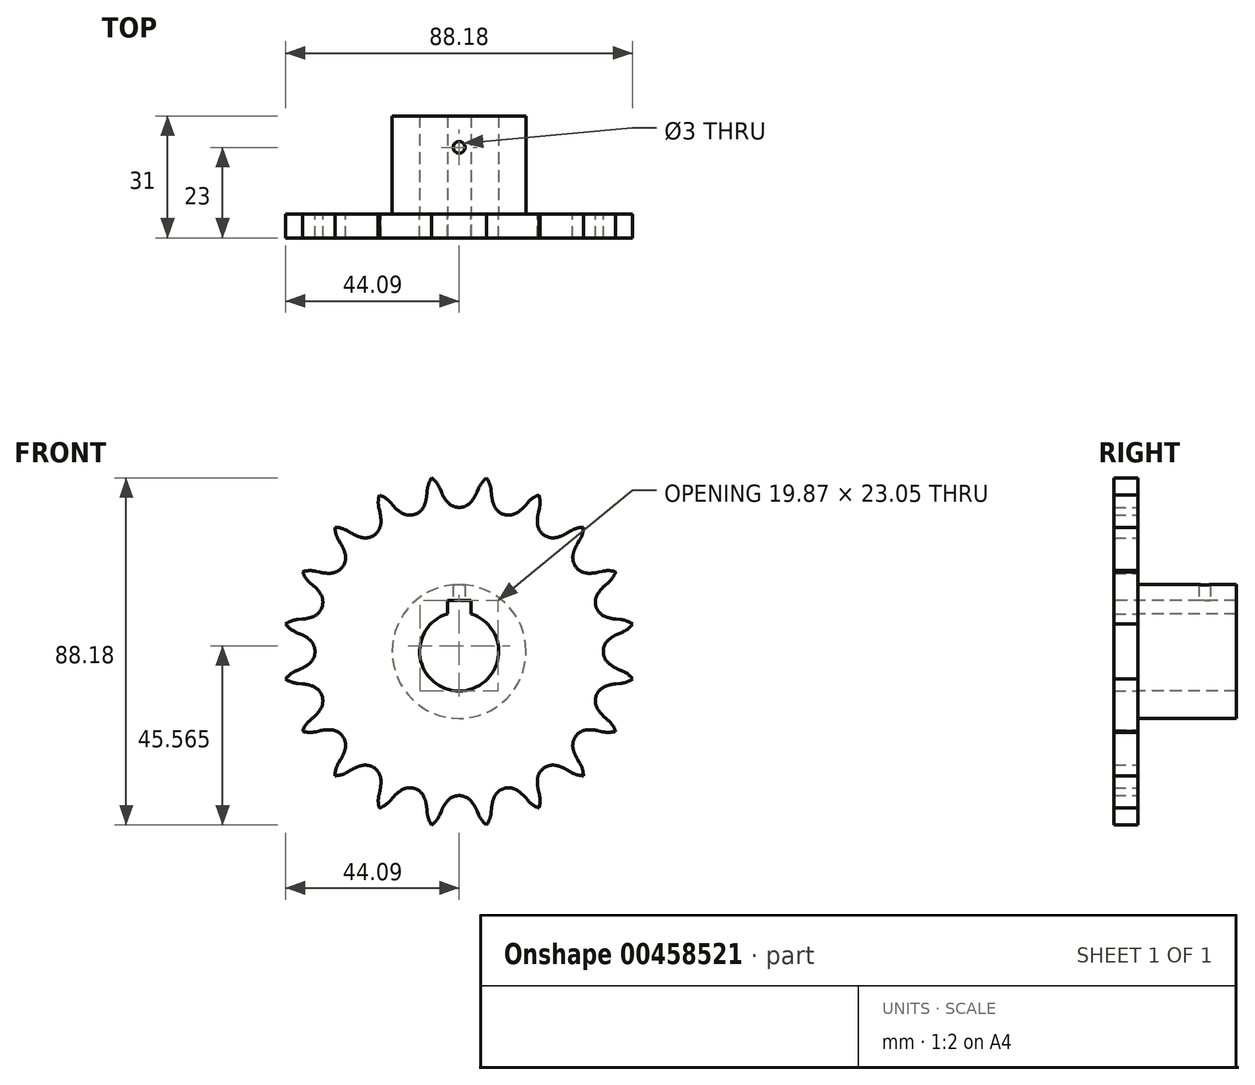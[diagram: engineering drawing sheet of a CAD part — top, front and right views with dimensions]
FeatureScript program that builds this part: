
annotation { "Feature Type Name" : "Feature", "Feature Type Description" : "" }
export const myFeature = defineFeature(function(context is Context, id is Id, definition is map)
    precondition{}
    {
        {
            var Q0;
            Q0=qCreatedBy(makeId("Front.planeOp"),FACE);
            var sketch = newSketch(context, id + "F0", { "sketchPlane" : qUnion([Q0])});
            skCircle(sketch, "E0", {"center": v(0, 0) * mm, "radius": 17 * mm});
            skCircle(sketch, "E1", {"center": v(0, 0) * mm, "radius": 10.05 * mm});
            skSolve(sketch);
        }
        {
            var Q0;
            Q0=makeQuery(id+"F0.imprint","IMPRINT",FACE,{"disambiguationData":[TD([[makeQuery(id+"F0.imprint","IMPRINT",EDGE,{"derivedFrom":sQuery(id+"F0.wireOp",EDGE,"E0")}),1.0]])]});
            extrude(context, id + "F1", {"entities" : qUnion([Q0]), "oppositeDirection" : true, "depth" : 25 * mm, "offsetDistance" : 25 * mm});
        }
        {
            var Q0;
            Q0=qCreatedBy(makeId("Front.planeOp"),FACE);
            var sketch = newSketch(context, id + "F2", { "sketchPlane" : qUnion([Q0])});
            skArc(sketch, "E2", {"start": v(-3.98, 40.72) * mm, "mid": v(-3.98, 40.56) * mm, "end": v(-3.98, 40.4) * mm, "construction": true});
            skLineSegment(sketch, "E3", {"start": v(0, 40.6) * mm, "end": v(37.9, 40.6) * mm, "construction": true});
            skLineSegment(sketch, "E4", {"start": v(0, 40.6) * mm, "end": v(5, 44.5) * mm, "construction": true});
            skLineSegment(sketch, "E5", {"start": v(5, 44.5) * mm, "end": v(2.7, 43.53) * mm, "construction": true});
            skLineSegment(sketch, "E6", {"start": v(-4.52, 40.5) * mm, "end": v(-4.9, 41.4) * mm});
            skArc(sketch, "E7", {"start": v(-4.9, 41.4) * mm, "mid": v(-5.76, 42.88) * mm, "end": v(-6.98, 44.09) * mm});
            skLineSegment(sketch, "E8", {"start": v(0, 0) * mm, "end": v(-11.22, 70.86) * mm, "construction": true});
            skArc(sketch, "E9.trimOffspring", {"start": v(-4.52, 40.5) * mm, "mid": v(-3.9, 39.27) * mm, "end": v(-3.14, 38.14) * mm});
            skArc(sketch, "E10.trimOffspring", {"start": v(3.14, 43.04) * mm, "mid": v(2.92, 43.3) * mm, "end": v(2.7, 43.53) * mm, "construction": true});
            skLineSegment(sketch, "E11", {"start": v(0, 40.6) * mm, "end": v(0, 32.99) * mm, "construction": true});
            skArc(sketch, "E12.trimOffspring", {"start": v(3.98, 40.4) * mm, "mid": v(3.98, 40.5) * mm, "end": v(3.98, 40.6) * mm, "construction": true});
            skArc(sketch, "E13.trimOffspring", {"start": v(-3.14, 38.14) * mm, "mid": v(-1.75, 37.01) * mm, "end": v(0, 36.61) * mm});
            skLineSegment(sketch, "E14.trimOffspring", {"start": v(-3.98, 40.72) * mm, "end": v(-4.52, 40.5) * mm, "construction": true});
            skArc(sketch, "E15.MirrorCS", {"start": v(3.14, 38.14) * mm, "mid": v(1.75, 37.01) * mm, "end": v(0, 36.61) * mm});
            skArc(sketch, "E16.MirrorCS", {"start": v(4.52, 40.5) * mm, "mid": v(3.9, 39.27) * mm, "end": v(3.14, 38.14) * mm});
            skArc(sketch, "E17.MirrorCS", {"start": v(4.9, 41.4) * mm, "mid": v(5.76, 42.88) * mm, "end": v(6.98, 44.09) * mm});
            skLineSegment(sketch, "E18.MirrorCS", {"start": v(4.52, 40.5) * mm, "end": v(4.9, 41.4) * mm});
            skArc(sketch, "E19.1.0", {"start": v(-8.13, 40.89) * mm, "mid": v(-7.77, 42.56) * mm, "end": v(-6.98, 44.09) * mm});
            skArc(sketch, "E19.1.1", {"start": v(-8.22, 39.9) * mm, "mid": v(-8.42, 38.56) * mm, "end": v(-8.8, 37.24) * mm});
            skArc(sketch, "E19.1.2", {"start": v(-8.8, 37.24) * mm, "mid": v(-9.78, 35.74) * mm, "end": v(-11.31, 34.82) * mm});
            skArc(sketch, "E19.1.3", {"start": v(-14.77, 35.3) * mm, "mid": v(-13.1, 34.66) * mm, "end": v(-11.31, 34.82) * mm});
            skArc(sketch, "E19.1.4", {"start": v(-16.81, 37.12) * mm, "mid": v(-15.85, 36.14) * mm, "end": v(-14.77, 35.3) * mm});
            skLineSegment(sketch, "E19.1.5", {"start": v(-16.81, 37.12) * mm, "end": v(-17.45, 37.86) * mm});
            skLineSegment(sketch, "E19.1.6", {"start": v(-8.22, 39.9) * mm, "end": v(-8.13, 40.89) * mm});
            skArc(sketch, "E19.1.7", {"start": v(-17.45, 37.86) * mm, "mid": v(-18.73, 39) * mm, "end": v(-20.26, 39.77) * mm});
            skArc(sketch, "E19.2.0", {"start": v(-20.37, 36.37) * mm, "mid": v(-20.54, 38.08) * mm, "end": v(-20.26, 39.77) * mm});
            skArc(sketch, "E19.2.1", {"start": v(-20.15, 35.42) * mm, "mid": v(-19.92, 34.07) * mm, "end": v(-19.88, 32.7) * mm});
            skArc(sketch, "E19.2.2", {"start": v(-19.88, 32.7) * mm, "mid": v(-20.34, 30.97) * mm, "end": v(-21.52, 29.62) * mm});
            skArc(sketch, "E19.2.3", {"start": v(-24.96, 29.01) * mm, "mid": v(-23.17, 28.92) * mm, "end": v(-21.52, 29.62) * mm});
            skArc(sketch, "E19.2.4", {"start": v(-27.46, 30.1) * mm, "mid": v(-26.24, 29.48) * mm, "end": v(-24.96, 29.01) * mm});
            skLineSegment(sketch, "E19.2.5", {"start": v(-27.46, 30.1) * mm, "end": v(-28.3, 30.61) * mm});
            skLineSegment(sketch, "E19.2.6", {"start": v(-20.15, 35.42) * mm, "end": v(-20.37, 36.37) * mm});
            skArc(sketch, "E19.2.7", {"start": v(-28.3, 30.61) * mm, "mid": v(-29.87, 31.3) * mm, "end": v(-31.56, 31.56) * mm});
            skArc(sketch, "E19.3.0", {"start": v(-30.61, 28.3) * mm, "mid": v(-31.3, 29.87) * mm, "end": v(-31.56, 31.56) * mm});
            skArc(sketch, "E19.3.1", {"start": v(-30.1, 27.46) * mm, "mid": v(-29.48, 26.24) * mm, "end": v(-29.01, 24.96) * mm});
            skArc(sketch, "E19.3.2", {"start": v(-29.01, 24.96) * mm, "mid": v(-28.92, 23.17) * mm, "end": v(-29.62, 21.52) * mm});
            skArc(sketch, "E19.3.3", {"start": v(-32.7, 19.88) * mm, "mid": v(-30.97, 20.34) * mm, "end": v(-29.62, 21.52) * mm});
            skArc(sketch, "E19.3.4", {"start": v(-35.42, 20.15) * mm, "mid": v(-34.07, 19.92) * mm, "end": v(-32.7, 19.88) * mm});
            skLineSegment(sketch, "E19.3.5", {"start": v(-35.42, 20.15) * mm, "end": v(-36.37, 20.37) * mm});
            skLineSegment(sketch, "E19.3.6", {"start": v(-30.1, 27.46) * mm, "end": v(-30.61, 28.3) * mm});
            skArc(sketch, "E19.3.7", {"start": v(-36.37, 20.37) * mm, "mid": v(-38.08, 20.54) * mm, "end": v(-39.77, 20.26) * mm});
            skArc(sketch, "E19.4.0", {"start": v(-37.86, 17.45) * mm, "mid": v(-39, 18.73) * mm, "end": v(-39.77, 20.26) * mm});
            skArc(sketch, "E19.4.1", {"start": v(-37.12, 16.81) * mm, "mid": v(-36.14, 15.85) * mm, "end": v(-35.3, 14.77) * mm});
            skArc(sketch, "E19.4.2", {"start": v(-35.3, 14.77) * mm, "mid": v(-34.66, 13.1) * mm, "end": v(-34.82, 11.31) * mm});
            skArc(sketch, "E19.4.3", {"start": v(-37.24, 8.8) * mm, "mid": v(-35.74, 9.78) * mm, "end": v(-34.82, 11.31) * mm});
            skArc(sketch, "E19.4.4", {"start": v(-39.9, 8.22) * mm, "mid": v(-38.56, 8.42) * mm, "end": v(-37.24, 8.8) * mm});
            skLineSegment(sketch, "E19.4.5", {"start": v(-39.9, 8.22) * mm, "end": v(-40.89, 8.13) * mm});
            skLineSegment(sketch, "E19.4.6", {"start": v(-37.12, 16.81) * mm, "end": v(-37.86, 17.45) * mm});
            skArc(sketch, "E19.4.7", {"start": v(-40.89, 8.13) * mm, "mid": v(-42.56, 7.77) * mm, "end": v(-44.09, 6.98) * mm});
            skArc(sketch, "E19.5.0", {"start": v(-41.4, 4.9) * mm, "mid": v(-42.88, 5.76) * mm, "end": v(-44.09, 6.98) * mm});
            skArc(sketch, "E19.5.1", {"start": v(-40.5, 4.52) * mm, "mid": v(-39.27, 3.9) * mm, "end": v(-38.14, 3.14) * mm});
            skArc(sketch, "E19.5.2", {"start": v(-38.14, 3.14) * mm, "mid": v(-37.01, 1.75) * mm, "end": v(-36.61, 0) * mm});
            skArc(sketch, "E19.5.3", {"start": v(-38.14, -3.14) * mm, "mid": v(-37.01, -1.75) * mm, "end": v(-36.61, 0) * mm});
            skArc(sketch, "E19.5.4", {"start": v(-40.5, -4.52) * mm, "mid": v(-39.27, -3.9) * mm, "end": v(-38.14, -3.14) * mm});
            skLineSegment(sketch, "E19.5.5", {"start": v(-40.5, -4.52) * mm, "end": v(-41.4, -4.9) * mm});
            skLineSegment(sketch, "E19.5.6", {"start": v(-40.5, 4.52) * mm, "end": v(-41.4, 4.9) * mm});
            skArc(sketch, "E19.5.7", {"start": v(-41.4, -4.9) * mm, "mid": v(-42.88, -5.76) * mm, "end": v(-44.09, -6.98) * mm});
            skArc(sketch, "E19.6.0", {"start": v(-40.89, -8.13) * mm, "mid": v(-42.56, -7.77) * mm, "end": v(-44.09, -6.98) * mm});
            skArc(sketch, "E19.6.1", {"start": v(-39.9, -8.22) * mm, "mid": v(-38.56, -8.42) * mm, "end": v(-37.24, -8.8) * mm});
            skArc(sketch, "E19.6.2", {"start": v(-37.24, -8.8) * mm, "mid": v(-35.74, -9.78) * mm, "end": v(-34.82, -11.31) * mm});
            skArc(sketch, "E19.6.3", {"start": v(-35.3, -14.77) * mm, "mid": v(-34.66, -13.1) * mm, "end": v(-34.82, -11.31) * mm});
            skArc(sketch, "E19.6.4", {"start": v(-37.12, -16.81) * mm, "mid": v(-36.14, -15.85) * mm, "end": v(-35.3, -14.77) * mm});
            skLineSegment(sketch, "E19.6.5", {"start": v(-37.12, -16.81) * mm, "end": v(-37.86, -17.45) * mm});
            skLineSegment(sketch, "E19.6.6", {"start": v(-39.9, -8.22) * mm, "end": v(-40.89, -8.13) * mm});
            skArc(sketch, "E19.6.7", {"start": v(-37.86, -17.45) * mm, "mid": v(-39, -18.73) * mm, "end": v(-39.77, -20.26) * mm});
            skArc(sketch, "E19.7.0", {"start": v(-36.37, -20.37) * mm, "mid": v(-38.08, -20.54) * mm, "end": v(-39.77, -20.26) * mm});
            skArc(sketch, "E19.7.1", {"start": v(-35.42, -20.15) * mm, "mid": v(-34.07, -19.92) * mm, "end": v(-32.7, -19.88) * mm});
            skArc(sketch, "E19.7.2", {"start": v(-32.7, -19.88) * mm, "mid": v(-30.97, -20.34) * mm, "end": v(-29.62, -21.52) * mm});
            skArc(sketch, "E19.7.3", {"start": v(-29.01, -24.96) * mm, "mid": v(-28.92, -23.17) * mm, "end": v(-29.62, -21.52) * mm});
            skArc(sketch, "E19.7.4", {"start": v(-30.1, -27.46) * mm, "mid": v(-29.48, -26.24) * mm, "end": v(-29.01, -24.96) * mm});
            skLineSegment(sketch, "E19.7.5", {"start": v(-30.1, -27.46) * mm, "end": v(-30.61, -28.3) * mm});
            skLineSegment(sketch, "E19.7.6", {"start": v(-35.42, -20.15) * mm, "end": v(-36.37, -20.37) * mm});
            skArc(sketch, "E19.7.7", {"start": v(-30.61, -28.3) * mm, "mid": v(-31.3, -29.87) * mm, "end": v(-31.56, -31.56) * mm});
            skArc(sketch, "E19.8.0", {"start": v(-28.3, -30.61) * mm, "mid": v(-29.87, -31.3) * mm, "end": v(-31.56, -31.56) * mm});
            skArc(sketch, "E19.8.1", {"start": v(-27.46, -30.1) * mm, "mid": v(-26.24, -29.48) * mm, "end": v(-24.96, -29.01) * mm});
            skArc(sketch, "E19.8.2", {"start": v(-24.96, -29.01) * mm, "mid": v(-23.17, -28.92) * mm, "end": v(-21.52, -29.62) * mm});
            skArc(sketch, "E19.8.3", {"start": v(-19.88, -32.7) * mm, "mid": v(-20.34, -30.97) * mm, "end": v(-21.52, -29.62) * mm});
            skArc(sketch, "E19.8.4", {"start": v(-20.15, -35.42) * mm, "mid": v(-19.92, -34.07) * mm, "end": v(-19.88, -32.7) * mm});
            skLineSegment(sketch, "E19.8.5", {"start": v(-20.15, -35.42) * mm, "end": v(-20.37, -36.37) * mm});
            skLineSegment(sketch, "E19.8.6", {"start": v(-27.46, -30.1) * mm, "end": v(-28.3, -30.61) * mm});
            skArc(sketch, "E19.8.7", {"start": v(-20.37, -36.37) * mm, "mid": v(-20.54, -38.08) * mm, "end": v(-20.26, -39.77) * mm});
            skArc(sketch, "E19.9.0", {"start": v(-17.45, -37.86) * mm, "mid": v(-18.73, -39) * mm, "end": v(-20.26, -39.77) * mm});
            skArc(sketch, "E19.9.1", {"start": v(-16.81, -37.12) * mm, "mid": v(-15.85, -36.14) * mm, "end": v(-14.77, -35.3) * mm});
            skArc(sketch, "E19.9.2", {"start": v(-14.77, -35.3) * mm, "mid": v(-13.1, -34.66) * mm, "end": v(-11.31, -34.82) * mm});
            skArc(sketch, "E19.9.3", {"start": v(-8.8, -37.24) * mm, "mid": v(-9.78, -35.74) * mm, "end": v(-11.31, -34.82) * mm});
            skArc(sketch, "E19.9.4", {"start": v(-8.22, -39.9) * mm, "mid": v(-8.42, -38.56) * mm, "end": v(-8.8, -37.24) * mm});
            skLineSegment(sketch, "E19.9.5", {"start": v(-8.22, -39.9) * mm, "end": v(-8.13, -40.89) * mm});
            skLineSegment(sketch, "E19.9.6", {"start": v(-16.81, -37.12) * mm, "end": v(-17.45, -37.86) * mm});
            skArc(sketch, "E19.9.7", {"start": v(-8.13, -40.89) * mm, "mid": v(-7.77, -42.56) * mm, "end": v(-6.98, -44.09) * mm});
            skArc(sketch, "E19.10.0", {"start": v(-4.9, -41.4) * mm, "mid": v(-5.76, -42.88) * mm, "end": v(-6.98, -44.09) * mm});
            skArc(sketch, "E19.10.1", {"start": v(-4.52, -40.5) * mm, "mid": v(-3.9, -39.27) * mm, "end": v(-3.14, -38.14) * mm});
            skArc(sketch, "E19.10.2", {"start": v(-3.14, -38.14) * mm, "mid": v(-1.75, -37.01) * mm, "end": v(0, -36.61) * mm});
            skArc(sketch, "E19.10.3", {"start": v(3.14, -38.14) * mm, "mid": v(1.75, -37.01) * mm, "end": v(0, -36.61) * mm});
            skArc(sketch, "E19.10.4", {"start": v(4.52, -40.5) * mm, "mid": v(3.9, -39.27) * mm, "end": v(3.14, -38.14) * mm});
            skLineSegment(sketch, "E19.10.5", {"start": v(4.52, -40.5) * mm, "end": v(4.9, -41.4) * mm});
            skLineSegment(sketch, "E19.10.6", {"start": v(-4.52, -40.5) * mm, "end": v(-4.9, -41.4) * mm});
            skArc(sketch, "E19.10.7", {"start": v(4.9, -41.4) * mm, "mid": v(5.76, -42.88) * mm, "end": v(6.98, -44.09) * mm});
            skArc(sketch, "E19.11.0", {"start": v(8.13, -40.89) * mm, "mid": v(7.77, -42.56) * mm, "end": v(6.98, -44.09) * mm});
            skArc(sketch, "E19.11.1", {"start": v(8.22, -39.9) * mm, "mid": v(8.42, -38.56) * mm, "end": v(8.8, -37.24) * mm});
            skArc(sketch, "E19.11.2", {"start": v(8.8, -37.24) * mm, "mid": v(9.78, -35.74) * mm, "end": v(11.31, -34.82) * mm});
            skArc(sketch, "E19.11.3", {"start": v(14.77, -35.3) * mm, "mid": v(13.1, -34.66) * mm, "end": v(11.31, -34.82) * mm});
            skArc(sketch, "E19.11.4", {"start": v(16.81, -37.12) * mm, "mid": v(15.85, -36.14) * mm, "end": v(14.77, -35.3) * mm});
            skLineSegment(sketch, "E19.11.5", {"start": v(16.81, -37.12) * mm, "end": v(17.45, -37.86) * mm});
            skLineSegment(sketch, "E19.11.6", {"start": v(8.22, -39.9) * mm, "end": v(8.13, -40.89) * mm});
            skArc(sketch, "E19.11.7", {"start": v(17.45, -37.86) * mm, "mid": v(18.73, -39) * mm, "end": v(20.26, -39.77) * mm});
            skArc(sketch, "E19.12.0", {"start": v(20.37, -36.37) * mm, "mid": v(20.54, -38.08) * mm, "end": v(20.26, -39.77) * mm});
            skArc(sketch, "E19.12.1", {"start": v(20.15, -35.42) * mm, "mid": v(19.92, -34.07) * mm, "end": v(19.88, -32.7) * mm});
            skArc(sketch, "E19.12.2", {"start": v(19.88, -32.7) * mm, "mid": v(20.34, -30.97) * mm, "end": v(21.52, -29.62) * mm});
            skArc(sketch, "E19.12.3", {"start": v(24.96, -29.01) * mm, "mid": v(23.17, -28.92) * mm, "end": v(21.52, -29.62) * mm});
            skArc(sketch, "E19.12.4", {"start": v(27.46, -30.1) * mm, "mid": v(26.24, -29.48) * mm, "end": v(24.96, -29.01) * mm});
            skLineSegment(sketch, "E19.12.5", {"start": v(27.46, -30.1) * mm, "end": v(28.3, -30.61) * mm});
            skLineSegment(sketch, "E19.12.6", {"start": v(20.15, -35.42) * mm, "end": v(20.37, -36.37) * mm});
            skArc(sketch, "E19.12.7", {"start": v(28.3, -30.61) * mm, "mid": v(29.87, -31.3) * mm, "end": v(31.56, -31.56) * mm});
            skArc(sketch, "E19.13.0", {"start": v(30.61, -28.3) * mm, "mid": v(31.3, -29.87) * mm, "end": v(31.56, -31.56) * mm});
            skArc(sketch, "E19.13.1", {"start": v(30.1, -27.46) * mm, "mid": v(29.48, -26.24) * mm, "end": v(29.01, -24.96) * mm});
            skArc(sketch, "E19.13.2", {"start": v(29.01, -24.96) * mm, "mid": v(28.92, -23.17) * mm, "end": v(29.62, -21.52) * mm});
            skArc(sketch, "E19.13.3", {"start": v(32.7, -19.88) * mm, "mid": v(30.97, -20.34) * mm, "end": v(29.62, -21.52) * mm});
            skArc(sketch, "E19.13.4", {"start": v(35.42, -20.15) * mm, "mid": v(34.07, -19.92) * mm, "end": v(32.7, -19.88) * mm});
            skLineSegment(sketch, "E19.13.5", {"start": v(35.42, -20.15) * mm, "end": v(36.37, -20.37) * mm});
            skLineSegment(sketch, "E19.13.6", {"start": v(30.1, -27.46) * mm, "end": v(30.61, -28.3) * mm});
            skArc(sketch, "E19.13.7", {"start": v(36.37, -20.37) * mm, "mid": v(38.08, -20.54) * mm, "end": v(39.77, -20.26) * mm});
            skArc(sketch, "E19.14.0", {"start": v(37.86, -17.45) * mm, "mid": v(39, -18.73) * mm, "end": v(39.77, -20.26) * mm});
            skArc(sketch, "E19.14.1", {"start": v(37.12, -16.81) * mm, "mid": v(36.14, -15.85) * mm, "end": v(35.3, -14.77) * mm});
            skArc(sketch, "E19.14.2", {"start": v(35.3, -14.77) * mm, "mid": v(34.66, -13.1) * mm, "end": v(34.82, -11.31) * mm});
            skArc(sketch, "E19.14.3", {"start": v(37.24, -8.8) * mm, "mid": v(35.74, -9.78) * mm, "end": v(34.82, -11.31) * mm});
            skArc(sketch, "E19.14.4", {"start": v(39.9, -8.22) * mm, "mid": v(38.56, -8.42) * mm, "end": v(37.24, -8.8) * mm});
            skLineSegment(sketch, "E19.14.5", {"start": v(39.9, -8.22) * mm, "end": v(40.89, -8.13) * mm});
            skLineSegment(sketch, "E19.14.6", {"start": v(37.12, -16.81) * mm, "end": v(37.86, -17.45) * mm});
            skArc(sketch, "E19.14.7", {"start": v(40.89, -8.13) * mm, "mid": v(42.56, -7.77) * mm, "end": v(44.09, -6.98) * mm});
            skArc(sketch, "E19.15.0", {"start": v(41.4, -4.9) * mm, "mid": v(42.88, -5.76) * mm, "end": v(44.09, -6.98) * mm});
            skArc(sketch, "E19.15.1", {"start": v(40.5, -4.52) * mm, "mid": v(39.27, -3.9) * mm, "end": v(38.14, -3.14) * mm});
            skArc(sketch, "E19.15.2", {"start": v(38.14, -3.14) * mm, "mid": v(37.01, -1.75) * mm, "end": v(36.61, 0) * mm});
            skArc(sketch, "E19.15.3", {"start": v(38.14, 3.14) * mm, "mid": v(37.01, 1.75) * mm, "end": v(36.61, 0) * mm});
            skArc(sketch, "E19.15.4", {"start": v(40.5, 4.52) * mm, "mid": v(39.27, 3.9) * mm, "end": v(38.14, 3.14) * mm});
            skLineSegment(sketch, "E19.15.5", {"start": v(40.5, 4.52) * mm, "end": v(41.4, 4.9) * mm});
            skLineSegment(sketch, "E19.15.6", {"start": v(40.5, -4.52) * mm, "end": v(41.4, -4.9) * mm});
            skArc(sketch, "E19.15.7", {"start": v(41.4, 4.9) * mm, "mid": v(42.88, 5.76) * mm, "end": v(44.09, 6.98) * mm});
            skArc(sketch, "E19.16.0", {"start": v(40.89, 8.13) * mm, "mid": v(42.56, 7.77) * mm, "end": v(44.09, 6.98) * mm});
            skArc(sketch, "E19.16.1", {"start": v(39.9, 8.22) * mm, "mid": v(38.56, 8.42) * mm, "end": v(37.24, 8.8) * mm});
            skArc(sketch, "E19.16.2", {"start": v(37.24, 8.8) * mm, "mid": v(35.74, 9.78) * mm, "end": v(34.82, 11.31) * mm});
            skArc(sketch, "E19.16.3", {"start": v(35.3, 14.77) * mm, "mid": v(34.66, 13.1) * mm, "end": v(34.82, 11.31) * mm});
            skArc(sketch, "E19.16.4", {"start": v(37.12, 16.81) * mm, "mid": v(36.14, 15.85) * mm, "end": v(35.3, 14.77) * mm});
            skLineSegment(sketch, "E19.16.5", {"start": v(37.12, 16.81) * mm, "end": v(37.86, 17.45) * mm});
            skLineSegment(sketch, "E19.16.6", {"start": v(39.9, 8.22) * mm, "end": v(40.89, 8.13) * mm});
            skArc(sketch, "E19.16.7", {"start": v(37.86, 17.45) * mm, "mid": v(39, 18.73) * mm, "end": v(39.77, 20.26) * mm});
            skArc(sketch, "E19.17.0", {"start": v(36.37, 20.37) * mm, "mid": v(38.08, 20.54) * mm, "end": v(39.77, 20.26) * mm});
            skArc(sketch, "E19.17.1", {"start": v(35.42, 20.15) * mm, "mid": v(34.07, 19.92) * mm, "end": v(32.7, 19.88) * mm});
            skArc(sketch, "E19.17.2", {"start": v(32.7, 19.88) * mm, "mid": v(30.97, 20.34) * mm, "end": v(29.62, 21.52) * mm});
            skArc(sketch, "E19.17.3", {"start": v(29.01, 24.96) * mm, "mid": v(28.92, 23.17) * mm, "end": v(29.62, 21.52) * mm});
            skArc(sketch, "E19.17.4", {"start": v(30.1, 27.46) * mm, "mid": v(29.48, 26.24) * mm, "end": v(29.01, 24.96) * mm});
            skLineSegment(sketch, "E19.17.5", {"start": v(30.1, 27.46) * mm, "end": v(30.61, 28.3) * mm});
            skLineSegment(sketch, "E19.17.6", {"start": v(35.42, 20.15) * mm, "end": v(36.37, 20.37) * mm});
            skArc(sketch, "E19.17.7", {"start": v(30.61, 28.3) * mm, "mid": v(31.3, 29.87) * mm, "end": v(31.56, 31.56) * mm});
            skArc(sketch, "E19.18.0", {"start": v(28.3, 30.61) * mm, "mid": v(29.87, 31.3) * mm, "end": v(31.56, 31.56) * mm});
            skArc(sketch, "E19.18.1", {"start": v(27.46, 30.1) * mm, "mid": v(26.24, 29.48) * mm, "end": v(24.96, 29.01) * mm});
            skArc(sketch, "E19.18.2", {"start": v(24.96, 29.01) * mm, "mid": v(23.17, 28.92) * mm, "end": v(21.52, 29.62) * mm});
            skArc(sketch, "E19.18.3", {"start": v(19.88, 32.7) * mm, "mid": v(20.34, 30.97) * mm, "end": v(21.52, 29.62) * mm});
            skArc(sketch, "E19.18.4", {"start": v(20.15, 35.42) * mm, "mid": v(19.92, 34.07) * mm, "end": v(19.88, 32.7) * mm});
            skLineSegment(sketch, "E19.18.5", {"start": v(20.15, 35.42) * mm, "end": v(20.37, 36.37) * mm});
            skLineSegment(sketch, "E19.18.6", {"start": v(27.46, 30.1) * mm, "end": v(28.3, 30.61) * mm});
            skArc(sketch, "E19.18.7", {"start": v(20.37, 36.37) * mm, "mid": v(20.54, 38.08) * mm, "end": v(20.26, 39.77) * mm});
            skArc(sketch, "E19.19.0", {"start": v(17.45, 37.86) * mm, "mid": v(18.73, 39) * mm, "end": v(20.26, 39.77) * mm});
            skArc(sketch, "E19.19.1", {"start": v(16.81, 37.12) * mm, "mid": v(15.85, 36.14) * mm, "end": v(14.77, 35.3) * mm});
            skArc(sketch, "E19.19.2", {"start": v(14.77, 35.3) * mm, "mid": v(13.1, 34.66) * mm, "end": v(11.31, 34.82) * mm});
            skArc(sketch, "E19.19.3", {"start": v(8.8, 37.24) * mm, "mid": v(9.78, 35.74) * mm, "end": v(11.31, 34.82) * mm});
            skArc(sketch, "E19.19.4", {"start": v(8.22, 39.9) * mm, "mid": v(8.42, 38.56) * mm, "end": v(8.8, 37.24) * mm});
            skLineSegment(sketch, "E19.19.5", {"start": v(8.22, 39.9) * mm, "end": v(8.13, 40.89) * mm});
            skLineSegment(sketch, "E19.19.6", {"start": v(16.81, 37.12) * mm, "end": v(17.45, 37.86) * mm});
            skArc(sketch, "E19.19.7", {"start": v(8.13, 40.89) * mm, "mid": v(7.77, 42.56) * mm, "end": v(6.98, 44.09) * mm});
            skPoint(sketch, "E19.center", {"position": v(0, 0) * mm});
            skCircle(sketch, "E20", {"center": v(0, 0) * mm, "radius": 10.04 * mm});
            skPoint(sketch, "E21.middle", {"position": v(0, 5.5) * mm});
            skSolve(sketch);
        }
        {
            var Q0;
            Q0 = qSketchRegion(id + "F2", true);
            extrude(context, id + "F3", {"entities" : qUnion([Q0]), "operationType" : NewBodyOperationType.ADD, "depth" : 6 * mm, "offsetDistance" : 25 * mm});
        }
        {
            var Q0;
            Q0=qCreatedBy(makeId("Front.planeOp"),FACE);
            var sketch = newSketch(context, id + "F4", { "sketchPlane" : qUnion([Q0])});
            skLineSegment(sketch, "E22.bottom", {"start": v(3, 7) * mm, "end": v(-3, 7) * mm});
            skLineSegment(sketch, "E22.top", {"start": v(3, 13) * mm, "end": v(-3, 13) * mm});
            skLineSegment(sketch, "E22.left", {"start": v(3, 7) * mm, "end": v(3, 13) * mm});
            skLineSegment(sketch, "E22.right", {"start": v(-3, 7) * mm, "end": v(-3, 13) * mm});
            skPoint(sketch, "E22.middle", {"position": v(0, 10) * mm});
            skSolve(sketch);
        }
        {
            var Q0;
            Q0=makeQuery(id+"F4.imprint","IMPRINT",FACE,{"disambiguationData":[TD([[makeQuery(id+"F4.imprint","IMPRINT",EDGE,{"derivedFrom":sQuery(id+"F4.wireOp",EDGE,"E22.bottom")}),-1.0]])]});
            extrude(context, id + "F5", {"entities" : qUnion([Q0]), "operationType" : NewBodyOperationType.REMOVE, "oppositeDirection" : true, "depth" : 76 * mm, "offsetDistance" : 25 * mm, "symmetric" : true});
        }
        {
            var Q0;
            Q0=qCreatedBy(makeId("Top.planeOp"),FACE);
            var sketch = newSketch(context, id + "F6", { "sketchPlane" : qUnion([Q0])});
            skLineSegment(sketch, "E23", {"start": v(0, 25) * mm, "end": v(0, 0) * mm, "construction": true});
            skCircle(sketch, "E24", {"center": v(0, 17) * mm, "radius": 1.5 * mm});
            skSolve(sketch);
        }
        {
            var Q0;
            Q0 = qSketchRegion(id + "F6", true);
            extrude(context, id + "F7", {"entities" : qUnion([Q0]), "operationType" : NewBodyOperationType.REMOVE, "depth" : 48.8 * mm, "offsetDistance" : 25 * mm});
        }
    });
